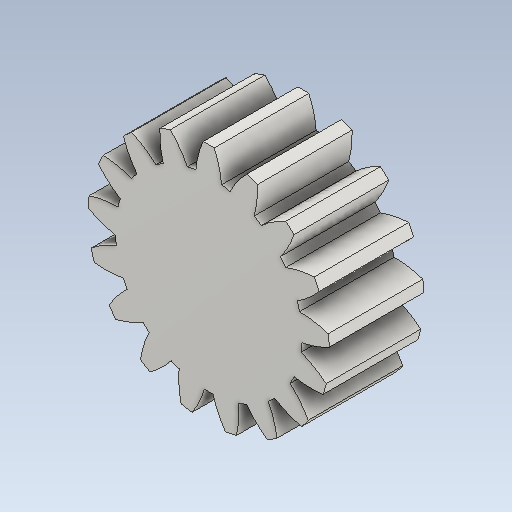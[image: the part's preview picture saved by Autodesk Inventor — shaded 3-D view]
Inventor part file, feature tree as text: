
AUTODESK INVENTOR PART (.ipt)
format: ipt  version: 2020 (Build 240168000, 168)  size: 242,176 bytes
history: native  units: mm (DEFAULTED — no unit token found)
features: plane x3, other x3, sketch x2, extrude x1
ambient origin geometry x8: Origin, YZ Plane, XZ Plane, XY Plane, X Axis, Y Axis, Z Axis, Center Point
bodies: Solid1 (feature_tree)
feature tree (9):
  extrude  "Extrusion1"  Depth=7.6mm TaperAngle=0.0deg
  plane  "Work Plane2"
  plane  "Work Plane8"
  plane  "Work Plane9"
  other  "Przekładnia walcowa"
  sketch  "Sketch1"  dims[d0=19.397123mm d1=7.6mm d2=0.0mm]
  sketch  "Sketch2"  dims[d3=17.447655mm d4=10.0mm d5=0.0mm d16=19.500321mm d17=0.0mm d34=1.847996mm d39=0.0mm d41=0.0mm d43=19.500321mm d46=19.500321mm d47=0.0mm d48=0.0mm]
  other  "Srf1"
  other  "Średnica podziałowa"
